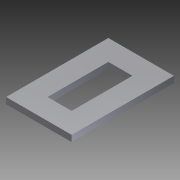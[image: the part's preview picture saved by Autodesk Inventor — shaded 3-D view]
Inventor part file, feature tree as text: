
AUTODESK INVENTOR PART (.ipt)
format: ipt  version: 2012 (Build 160160000, 160)  size: 74,240 bytes
history: native  units: mm
features: extrude x1, sketch x1
ambient origin geometry x8: Origin, YZ Plane, XZ Plane, XY Plane, X Axis, Y Axis, Z Axis, Center Point
bodies: Solid1 (feature_tree)
feature tree (2):
  extrude  "Extrusion1"  Depth=10.0mm
  sketch  "Sketch1"  dims[d1=29.3mm d5=11.6mm d8=10.0mm d9=3.0mm d10=0.0mm]
